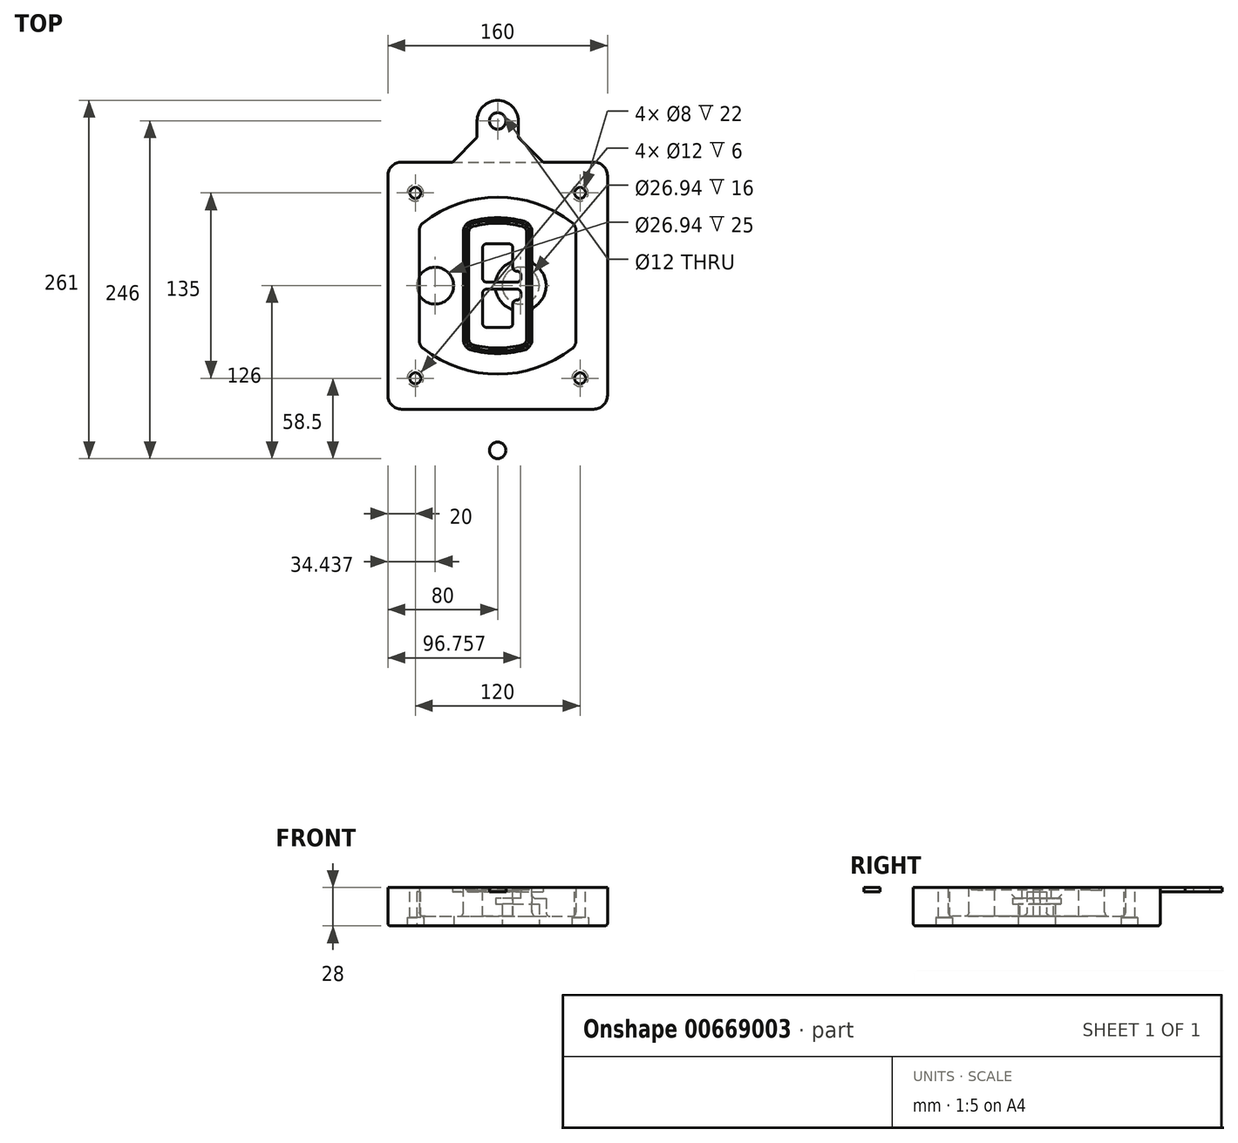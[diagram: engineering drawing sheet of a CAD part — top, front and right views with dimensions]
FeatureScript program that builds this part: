
annotation { "Feature Type Name" : "Feature", "Feature Type Description" : "" }
export const myFeature = defineFeature(function(context is Context, id is Id, definition is map)
    precondition{}
    {
        {
            var Q0;
            Q0=qCreatedBy(makeId("Top.planeOp"),FACE);
            var sketch = newSketch(context, id + "F0", { "sketchPlane" : qUnion([Q0])});
            skPoint(sketch, "E0.rect.middle", {"position": v(0, 0) * mm});
            skLineSegment(sketch, "E1.bottom", {"start": v(-70, -90) * mm, "end": v(70, -90) * mm});
            skLineSegment(sketch, "E1.top", {"start": v(-70, 90) * mm, "end": v(70, 90) * mm});
            skLineSegment(sketch, "E1.left", {"start": v(-80, -80) * mm, "end": v(-80, 80) * mm});
            skLineSegment(sketch, "E1.right", {"start": v(80, -80) * mm, "end": v(80, 80) * mm});
            skLineSegment(sketch, "E2", {"start": v(-80, 90) * mm, "end": v(80, -90) * mm, "construction": true});
            skLineSegment(sketch, "E3", {"start": v(80, 90) * mm, "end": v(-80, -90) * mm, "construction": true});
            skCircle(sketch, "E4", {"center": v(-60, 67.5) * mm, "radius": 4 * mm});
            skCircle(sketch, "E5", {"center": v(60, 67.5) * mm, "radius": 4 * mm});
            skCircle(sketch, "E6", {"center": v(60, -67.5) * mm, "radius": 4 * mm});
            skCircle(sketch, "E7", {"center": v(-60, -67.5) * mm, "radius": 4 * mm});
            skLineSegment(sketch, "E8", {"start": v(-60, 67.5) * mm, "end": v(60, 67.5) * mm, "construction": true});
            skLineSegment(sketch, "E9", {"start": v(60, 67.5) * mm, "end": v(60, -67.5) * mm, "construction": true});
            skLineSegment(sketch, "E10", {"start": v(60, -67.5) * mm, "end": v(-60, -67.5) * mm, "construction": true});
            skLineSegment(sketch, "E11", {"start": v(-60, -67.5) * mm, "end": v(-60, 67.5) * mm, "construction": true});
            skLineSegment(sketch, "E12", {"start": v(-60, 40.3) * mm, "end": v(-60, -40.3) * mm});
            skLineSegment(sketch, "E13", {"start": v(60, 40.3) * mm, "end": v(60, -40.3) * mm});
            skArc(sketch, "E14", {"start": v(56.15, 48.18) * mm, "mid": v(0, 67.5) * mm, "end": v(-56.15, 48.18) * mm});
            skArc(sketch, "E15", {"start": v(-56.15, -48.18) * mm, "mid": v(0, -67.5) * mm, "end": v(56.15, -48.18) * mm});
            skLineSegment(sketch, "E16", {"start": v(-60, 0) * mm, "end": v(60, 0) * mm, "construction": true});
            skPoint(sketch, "E17.visualSharp", {"position": v(-60, -45) * mm});
            skArc(sketch, "E17.filletArc", {"start": v(-60, -40.3) * mm, "mid": v(-58.99, -44.68) * mm, "end": v(-56.15, -48.18) * mm});
            skPoint(sketch, "E18.visualSharp", {"position": v(-60, 45) * mm});
            skArc(sketch, "E18.filletArc", {"start": v(-56.15, 48.18) * mm, "mid": v(-58.99, 44.68) * mm, "end": v(-60, 40.3) * mm});
            skPoint(sketch, "E19.visualSharp", {"position": v(60, 45) * mm});
            skArc(sketch, "E19.filletArc", {"start": v(60, 40.3) * mm, "mid": v(58.99, 44.68) * mm, "end": v(56.15, 48.18) * mm});
            skPoint(sketch, "E20.visualSharp", {"position": v(60, -45) * mm});
            skArc(sketch, "E20.filletArc", {"start": v(56.15, -48.18) * mm, "mid": v(58.99, -44.68) * mm, "end": v(60, -40.3) * mm});
            skPoint(sketch, "E21.visualSharp", {"position": v(-80, 90) * mm});
            skArc(sketch, "E21.filletArc", {"start": v(-70, 90) * mm, "mid": v(-77.07, 87.07) * mm, "end": v(-80, 80) * mm});
            skPoint(sketch, "E22.visualSharp", {"position": v(80, 90) * mm});
            skArc(sketch, "E22.filletArc", {"start": v(80, 80) * mm, "mid": v(77.07, 87.07) * mm, "end": v(70, 90) * mm});
            skPoint(sketch, "E23.visualSharp", {"position": v(80, -90) * mm});
            skArc(sketch, "E23.filletArc", {"start": v(70, -90) * mm, "mid": v(77.07, -87.07) * mm, "end": v(80, -80) * mm});
            skPoint(sketch, "E24.visualSharp", {"position": v(-80, -90) * mm});
            skArc(sketch, "E24.filletArc", {"start": v(-80, -80) * mm, "mid": v(-77.07, -87.07) * mm, "end": v(-70, -90) * mm});
            skArc(sketch, "E25.0", {"start": v(57, 40.3) * mm, "mid": v(56.3, 43.36) * mm, "end": v(54.3, 45.81) * mm});
            skLineSegment(sketch, "E25.1", {"start": v(57, 40.3) * mm, "end": v(57, -40.3) * mm});
            skArc(sketch, "E25.2", {"start": v(54.3, -45.81) * mm, "mid": v(56.3, -43.36) * mm, "end": v(57, -40.3) * mm});
            skArc(sketch, "E25.3", {"start": v(-54.3, -45.81) * mm, "mid": v(0, -64.5) * mm, "end": v(54.3, -45.81) * mm});
            skArc(sketch, "E25.4", {"start": v(-57, -40.3) * mm, "mid": v(-56.3, -43.36) * mm, "end": v(-54.3, -45.81) * mm});
            skArc(sketch, "E25.5", {"start": v(54.3, 45.81) * mm, "mid": v(0, 64.5) * mm, "end": v(-54.3, 45.81) * mm});
            skLineSegment(sketch, "E25.6", {"start": v(-57, 40.3) * mm, "end": v(-57, -40.3) * mm});
            skArc(sketch, "E25.7", {"start": v(-54.3, 45.81) * mm, "mid": v(-56.3, 43.36) * mm, "end": v(-57, 40.3) * mm});
            skArc(sketch, "E26.0", {"start": v(-58.62, 51.33) * mm, "mid": v(-62.58, 46.43) * mm, "end": v(-64, 40.3) * mm});
            skArc(sketch, "E26.1", {"start": v(58.62, 51.33) * mm, "mid": v(0, 71.5) * mm, "end": v(-58.62, 51.33) * mm});
            skArc(sketch, "E26.2", {"start": v(64, 40.3) * mm, "mid": v(62.58, 46.43) * mm, "end": v(58.62, 51.33) * mm});
            skLineSegment(sketch, "E26.3", {"start": v(64, 40.3) * mm, "end": v(64, -40.3) * mm});
            skArc(sketch, "E26.4", {"start": v(58.62, -51.33) * mm, "mid": v(62.58, -46.43) * mm, "end": v(64, -40.3) * mm});
            skLineSegment(sketch, "E26.5", {"start": v(-64, 40.3) * mm, "end": v(-64, -40.3) * mm});
            skArc(sketch, "E26.6", {"start": v(-58.62, -51.33) * mm, "mid": v(0, -71.5) * mm, "end": v(58.62, -51.33) * mm});
            skArc(sketch, "E26.7", {"start": v(-64, -40.3) * mm, "mid": v(-62.58, -46.43) * mm, "end": v(-58.62, -51.33) * mm});
            skSolve(sketch);
        }
        {
            var Q0;
            Q0=makeQuery(id+"F0.imprint","IMPRINT",FACE,{"disambiguationData":[TD([[makeQuery(id+"F0.imprint","IMPRINT",EDGE,{"derivedFrom":sQuery(id+"F0.wireOp",EDGE,"E1.bottom")}),1.0]])]});
            var Q1;
            Q1=makeQuery(id+"F0.imprint","IMPRINT",FACE,{"disambiguationData":[TD([[makeQuery(id+"F0.imprint","IMPRINT",EDGE,{"derivedFrom":sQuery(id+"F0.wireOp",EDGE,"E12")}),1.0]])]});
            var Q2;
            Q2=makeQuery(id+"F0.imprint","IMPRINT",FACE,{"disambiguationData":[TD([[makeQuery(id+"F0.imprint","IMPRINT",EDGE,{"derivedFrom":sQuery(id+"F0.wireOp",EDGE,"E25.0")}),1.0]])]});
            var Q3;
            Q3=makeQuery(id+"F0.imprint","IMPRINT",FACE,{"disambiguationData":[TD([[makeQuery(id+"F0.imprint","IMPRINT",EDGE,{"derivedFrom":sQuery(id+"F0.wireOp",EDGE,"E12")}),-1.0]])]});
            extrude(context, id + "F1", {"entities" : qUnion([Q0, Q1, Q2, Q3]), "oppositeDirection" : true, "depth" : 25 * mm});
        }
        {
            var Q0;
            Q0=makeQuery(id+"F0.imprint","IMPRINT",FACE,{"disambiguationData":[TD([[makeQuery(id+"F0.imprint","IMPRINT",EDGE,{"derivedFrom":sQuery(id+"F0.wireOp",EDGE,"E12")}),1.0]])]});
            extrude(context, id + "F2", {"entities" : qUnion([Q0]), "operationType" : NewBodyOperationType.ADD, "depth" : 3 * mm});
        }
        {
            var Q0;
            Q0=makeQuery(id+"F0.imprint","IMPRINT",FACE,{"disambiguationData":[TD([[makeQuery(id+"F0.imprint","IMPRINT",EDGE,{"derivedFrom":sQuery(id+"F0.wireOp",EDGE,"E25.0")}),1.0]])]});
            extrude(context, id + "F3", {"entities" : qUnion([Q0]), "operationType" : NewBodyOperationType.REMOVE, "oppositeDirection" : true, "depth" : 18 * mm});
        }
        {
            var Q0;
            Q0=makeQuery(id+"F2.opExtrude","CAP_FACE",FACE,{"disambiguationData":[OSD([sQuery(id+"F0.wireOp",EDGE,"E12"),sQuery(id+"F0.wireOp",EDGE,"E13"),sQuery(id+"F0.wireOp",EDGE,"E14"),sQuery(id+"F0.wireOp",EDGE,"E15"),sQuery(id+"F0.wireOp",EDGE,"E17.filletArc"),sQuery(id+"F0.wireOp",EDGE,"E18.filletArc"),sQuery(id+"F0.wireOp",EDGE,"E19.filletArc"),sQuery(id+"F0.wireOp",EDGE,"E20.filletArc"),sQuery(id+"F0.wireOp",EDGE,"E25.0"),sQuery(id+"F0.wireOp",EDGE,"E25.1"),sQuery(id+"F0.wireOp",EDGE,"E25.2"),sQuery(id+"F0.wireOp",EDGE,"E25.3"),sQuery(id+"F0.wireOp",EDGE,"E25.4"),sQuery(id+"F0.wireOp",EDGE,"E25.5"),sQuery(id+"F0.wireOp",EDGE,"E25.6"),sQuery(id+"F0.wireOp",EDGE,"E25.7")])],"isStart":false});
            var sketch = newSketch(context, id + "F4", { "sketchPlane" : qUnion([Q0])});
            skArc(sketch, "E27.0", {"start": v(-19.08, -46.97) * mm, "mid": v(0, -49.5) * mm, "end": v(19.08, -46.97) * mm});
            skArc(sketch, "E28.0", {"start": v(19.08, 46.97) * mm, "mid": v(0, 49.5) * mm, "end": v(-19.08, 46.97) * mm});
            skLineSegment(sketch, "E29", {"start": v(-25, 39.25) * mm, "end": v(-25, -39.25) * mm});
            skLineSegment(sketch, "E30", {"start": v(25, 39.25) * mm, "end": v(25, -39.25) * mm});
            skLineSegment(sketch, "E31", {"start": v(-25, 45.1) * mm, "end": v(25, 45.1) * mm, "construction": true});
            skLineSegment(sketch, "E32", {"start": v(-25, -45.1) * mm, "end": v(25, -45.1) * mm, "construction": true});
            skPoint(sketch, "E33.visualSharp", {"position": v(-25, 45.1) * mm});
            skArc(sketch, "E33.filletArc", {"start": v(-19.08, 46.97) * mm, "mid": v(-23.35, 44.11) * mm, "end": v(-25, 39.25) * mm});
            skPoint(sketch, "E34.visualSharp", {"position": v(25, 45.1) * mm});
            skArc(sketch, "E34.filletArc", {"start": v(25, 39.25) * mm, "mid": v(23.35, 44.11) * mm, "end": v(19.08, 46.97) * mm});
            skPoint(sketch, "E35.visualSharp", {"position": v(25, -45.1) * mm});
            skArc(sketch, "E35.filletArc", {"start": v(19.08, -46.97) * mm, "mid": v(23.35, -44.11) * mm, "end": v(25, -39.25) * mm});
            skPoint(sketch, "E36.visualSharp", {"position": v(-25, -45.1) * mm});
            skArc(sketch, "E36.filletArc", {"start": v(-25, -39.25) * mm, "mid": v(-23.35, -44.11) * mm, "end": v(-19.08, -46.97) * mm});
            skArc(sketch, "E37.0", {"start": v(54.3, 45.81) * mm, "mid": v(0, 64.5) * mm, "end": v(-54.3, 45.81) * mm});
            skArc(sketch, "E37.1", {"start": v(-54.3, 45.81) * mm, "mid": v(-56.3, 43.36) * mm, "end": v(-57, 40.3) * mm});
            skLineSegment(sketch, "E37.2", {"start": v(-57, 40.3) * mm, "end": v(-57, -40.3) * mm});
            skArc(sketch, "E37.3", {"start": v(-57, -40.3) * mm, "mid": v(-56.3, -43.36) * mm, "end": v(-54.3, -45.81) * mm});
            skArc(sketch, "E37.4", {"start": v(-54.3, -45.81) * mm, "mid": v(0, -64.5) * mm, "end": v(54.3, -45.81) * mm});
            skArc(sketch, "E37.5", {"start": v(54.3, -45.81) * mm, "mid": v(56.3, -43.36) * mm, "end": v(57, -40.3) * mm});
            skLineSegment(sketch, "E37.6", {"start": v(57, 40.3) * mm, "end": v(57, -40.3) * mm});
            skArc(sketch, "E37.7", {"start": v(57, 40.3) * mm, "mid": v(56.3, 43.36) * mm, "end": v(54.3, 45.81) * mm});
            skLineSegment(sketch, "E38.0", {"start": v(23, 39.25) * mm, "end": v(23, -39.25) * mm});
            skArc(sketch, "E38.1", {"start": v(18.56, -45.04) * mm, "mid": v(21.76, -42.9) * mm, "end": v(23, -39.25) * mm});
            skArc(sketch, "E38.2", {"start": v(-18.56, -45.04) * mm, "mid": v(0, -47.5) * mm, "end": v(18.56, -45.04) * mm});
            skArc(sketch, "E38.3", {"start": v(-23, -39.25) * mm, "mid": v(-21.76, -42.9) * mm, "end": v(-18.56, -45.04) * mm});
            skLineSegment(sketch, "E38.4", {"start": v(-23, 39.25) * mm, "end": v(-23, -39.25) * mm});
            skArc(sketch, "E38.5", {"start": v(23, 39.25) * mm, "mid": v(21.76, 42.9) * mm, "end": v(18.56, 45.04) * mm});
            skArc(sketch, "E38.6", {"start": v(-18.56, 45.04) * mm, "mid": v(-21.76, 42.9) * mm, "end": v(-23, 39.25) * mm});
            skArc(sketch, "E38.7", {"start": v(18.56, 45.04) * mm, "mid": v(0, 47.5) * mm, "end": v(-18.56, 45.04) * mm});
            skArc(sketch, "E39.0", {"start": v(21, 39.25) * mm, "mid": v(20.18, 41.68) * mm, "end": v(18.04, 43.1) * mm});
            skLineSegment(sketch, "E39.1", {"start": v(21, 39.25) * mm, "end": v(21, -39.25) * mm});
            skArc(sketch, "E39.2", {"start": v(18.04, -43.1) * mm, "mid": v(20.18, -41.68) * mm, "end": v(21, -39.25) * mm});
            skArc(sketch, "E39.3", {"start": v(-18.04, -43.1) * mm, "mid": v(0, -45.5) * mm, "end": v(18.04, -43.1) * mm});
            skArc(sketch, "E39.4", {"start": v(-21, -39.25) * mm, "mid": v(-20.18, -41.68) * mm, "end": v(-18.04, -43.1) * mm});
            skArc(sketch, "E39.5", {"start": v(18.04, 43.1) * mm, "mid": v(0, 45.5) * mm, "end": v(-18.04, 43.1) * mm});
            skLineSegment(sketch, "E39.6", {"start": v(-21, 39.25) * mm, "end": v(-21, -39.25) * mm});
            skArc(sketch, "E39.7", {"start": v(-18.04, 43.1) * mm, "mid": v(-20.18, 41.68) * mm, "end": v(-21, 39.25) * mm});
            skLineSegment(sketch, "E40", {"start": v(-25, 0) * mm, "end": v(25, 0) * mm, "construction": true});
            skLineSegment(sketch, "E41", {"start": v(-11, 5.5) * mm, "end": v(-11, 27.5) * mm});
            skLineSegment(sketch, "E42", {"start": v(-8, 30.5) * mm, "end": v(8, 30.5) * mm});
            skLineSegment(sketch, "E43", {"start": v(11, 27.5) * mm, "end": v(11, 13.5) * mm});
            skLineSegment(sketch, "E44", {"start": v(14, 10.5) * mm, "end": v(14, 10.5) * mm});
            skLineSegment(sketch, "E45", {"start": v(17, 7.5) * mm, "end": v(17, 5.5) * mm});
            skLineSegment(sketch, "E46", {"start": v(14, 2.5) * mm, "end": v(-8, 2.5) * mm});
            skPoint(sketch, "E47.visualSharp", {"position": v(-11, 30.5) * mm});
            skArc(sketch, "E47.filletArc", {"start": v(-8, 30.5) * mm, "mid": v(-10.12, 29.62) * mm, "end": v(-11, 27.5) * mm});
            skPoint(sketch, "E48.visualSharp", {"position": v(11, 30.5) * mm});
            skArc(sketch, "E48.filletArc", {"start": v(11, 27.5) * mm, "mid": v(10.12, 29.62) * mm, "end": v(8, 30.5) * mm});
            skPoint(sketch, "E49.visualSharp", {"position": v(11, 10.5) * mm});
            skArc(sketch, "E49.filletArc", {"start": v(11, 13.5) * mm, "mid": v(11.88, 11.38) * mm, "end": v(14, 10.5) * mm});
            skPoint(sketch, "E50.visualSharp", {"position": v(17, 10.5) * mm});
            skArc(sketch, "E50.filletArc", {"start": v(17, 7.5) * mm, "mid": v(16.12, 9.62) * mm, "end": v(14, 10.5) * mm});
            skPoint(sketch, "E51.visualSharp", {"position": v(17, 2.5) * mm});
            skArc(sketch, "E51.filletArc", {"start": v(14, 2.5) * mm, "mid": v(16.12, 3.38) * mm, "end": v(17, 5.5) * mm});
            skPoint(sketch, "E52.visualSharp", {"position": v(-11, 2.5) * mm});
            skArc(sketch, "E52.filletArc", {"start": v(-11, 5.5) * mm, "mid": v(-10.12, 3.38) * mm, "end": v(-8, 2.5) * mm});
            skLineSegment(sketch, "E53.0.MirrorCS", {"start": v(14, -2.5) * mm, "end": v(-8, -2.5) * mm});
            skArc(sketch, "E54.0.MirrorCS", {"start": v(-11, -5.5) * mm, "mid": v(-10.12, -3.38) * mm, "end": v(-8, -2.5) * mm});
            skLineSegment(sketch, "E55.0.MirrorCS", {"start": v(-11, -5.5) * mm, "end": v(-11, -27.5) * mm});
            skArc(sketch, "E56.0.MirrorCS", {"start": v(-8, -30.5) * mm, "mid": v(-10.12, -29.62) * mm, "end": v(-11, -27.5) * mm});
            skLineSegment(sketch, "E57.0.MirrorCS", {"start": v(-8, -30.5) * mm, "end": v(8, -30.5) * mm});
            skArc(sketch, "E58.0.MirrorCS", {"start": v(11, -27.5) * mm, "mid": v(10.12, -29.62) * mm, "end": v(8, -30.5) * mm});
            skLineSegment(sketch, "E59.0.MirrorCS", {"start": v(11, -27.5) * mm, "end": v(11, -13.5) * mm});
            skArc(sketch, "E60.0.MirrorCS", {"start": v(11, -13.5) * mm, "mid": v(11.88, -11.38) * mm, "end": v(14, -10.5) * mm});
            skArc(sketch, "E61.0.MirrorCS", {"start": v(17, -7.5) * mm, "mid": v(16.12, -9.62) * mm, "end": v(14, -10.5) * mm});
            skLineSegment(sketch, "E62.0.MirrorCS", {"start": v(17, -7.5) * mm, "end": v(17, -5.5) * mm});
            skArc(sketch, "E63.0.MirrorCS", {"start": v(14, -2.5) * mm, "mid": v(16.12, -3.38) * mm, "end": v(17, -5.5) * mm});
            skSolve(sketch);
        }
        {
            var Q0;
            Q0=makeQuery(id+"F4.imprint","IMPRINT",FACE,{"disambiguationData":[TD([[makeQuery(id+"F4.imprint","IMPRINT",EDGE,{"derivedFrom":sQuery(id+"F4.wireOp",EDGE,"E27.0")}),1.0]])]});
            var Q1;
            Q1=makeQuery(id+"F4.imprint","IMPRINT",FACE,{"disambiguationData":[TD([[makeQuery(id+"F4.imprint","IMPRINT",EDGE,{"derivedFrom":sQuery(id+"F4.wireOp",EDGE,"E38.0")}),-1.0]])]});
            var Q2;
            Q2=makeQuery(id+"F4.imprint","IMPRINT",FACE,{"disambiguationData":[TD([[makeQuery(id+"F4.imprint","IMPRINT",EDGE,{"derivedFrom":sQuery(id+"F4.wireOp",EDGE,"E39.0")}),1.0]])]});
            extrude(context, id + "F5", {"entities" : qUnion([Q0, Q1, Q2]), "operationType" : NewBodyOperationType.ADD, "endBound" : BoundingType.UP_TO_NEXT, "oppositeDirection" : true, "depth" : 25 * mm});
        }
        {
            var Q0;
            Q0=makeQuery(id+"F4.imprint","IMPRINT",FACE,{"disambiguationData":[TD([[makeQuery(id+"F4.imprint","IMPRINT",EDGE,{"derivedFrom":sQuery(id+"F4.wireOp",EDGE,"E38.0")}),-1.0]])]});
            extrude(context, id + "F6", {"entities" : qUnion([Q0]), "operationType" : NewBodyOperationType.REMOVE, "oppositeDirection" : true, "depth" : 2 * mm});
        }
        {
            var Q0;
            Q0=makeQuery(id+"F1.opExtrude","CAP_FACE",FACE,{"disambiguationData":[OSD([sQuery(id+"F0.wireOp",EDGE,"E1.bottom"),sQuery(id+"F0.wireOp",EDGE,"E1.top"),sQuery(id+"F0.wireOp",EDGE,"E1.left"),sQuery(id+"F0.wireOp",EDGE,"E1.right"),sQuery(id+"F0.wireOp",EDGE,"E4"),sQuery(id+"F0.wireOp",EDGE,"E5"),sQuery(id+"F0.wireOp",EDGE,"E6"),sQuery(id+"F0.wireOp",EDGE,"E7"),sQuery(id+"F0.wireOp",EDGE,"E21.filletArc"),sQuery(id+"F0.wireOp",EDGE,"E22.filletArc"),sQuery(id+"F0.wireOp",EDGE,"E23.filletArc"),sQuery(id+"F0.wireOp",EDGE,"E24.filletArc")])],"isStart":false});
            var sketch = newSketch(context, id + "F7", { "sketchPlane" : qUnion([Q0])});
            skCircle(sketch, "E64", {"center": v(16.76, 0) * mm, "radius": 13.47 * mm});
            skCircle(sketch, "E65", {"center": v(-45.56, 0) * mm, "radius": 13.47 * mm});
            skLineSegment(sketch, "E66", {"start": v(80, 0) * mm, "end": v(-80, 0) * mm});
            skCircle(sketch, "E67", {"center": v(16.76, 0) * mm, "radius": 18.47 * mm});
            skCircle(sketch, "E68", {"center": v(60, -67.5) * mm, "radius": 6 * mm});
            skCircle(sketch, "E69", {"center": v(-60, -67.5) * mm, "radius": 6 * mm});
            skCircle(sketch, "E70", {"center": v(-60, 67.5) * mm, "radius": 6 * mm});
            skCircle(sketch, "E71", {"center": v(60, 67.5) * mm, "radius": 6 * mm});
            skSolve(sketch);
        }
        {
            var Q0;
            {var subQ1=sQuery(id+"F7.wireOp",EDGE,"E66");var subQ4=sQuery(id+"F7.wireOp",EDGE,"E64");var subQ6=makeQuery(id+"F7.imprint","INTERSECT",VERTEX,{"disambiguationData":[OD(0.0)],"derivedFrom":[subQ4,subQ1]});Q0=makeQuery(id+"F7.imprint","IMPRINT",FACE,{"disambiguationData":[TD([[makeQuery(id+"F7.imprint","IMPRINT",EDGE,{"disambiguationData":[TD([[subQ6,-1.0]])],"derivedFrom":subQ4}),-1.0]])]});}
            var Q1;
            {var subQ0=sQuery(id+"F7.wireOp",EDGE,"E66");var subQ1=sQuery(id+"F7.wireOp",EDGE,"E64");var subQ3=makeQuery(id+"F7.imprint","INTERSECT",VERTEX,{"disambiguationData":[OD(0.0)],"derivedFrom":[subQ1,subQ0]});Q1=makeQuery(id+"F7.imprint","IMPRINT",FACE,{"disambiguationData":[TD([[makeQuery(id+"F7.imprint","IMPRINT",EDGE,{"disambiguationData":[TD([[subQ3,-1.0]])],"derivedFrom":subQ1}),1.0]])]});}
            var Q2;
            {var subQ0=sQuery(id+"F7.wireOp",EDGE,"E66");var subQ1=sQuery(id+"F7.wireOp",EDGE,"E64");var subQ3=makeQuery(id+"F7.imprint","INTERSECT",VERTEX,{"disambiguationData":[OD(0.0)],"derivedFrom":[subQ1,subQ0]});Q2=makeQuery(id+"F7.imprint","IMPRINT",FACE,{"disambiguationData":[TD([[makeQuery(id+"F7.imprint","IMPRINT",EDGE,{"disambiguationData":[TD([[subQ3,1.0]])],"derivedFrom":subQ1}),1.0]])]});}
            var Q3;
            {var subQ1=sQuery(id+"F7.wireOp",EDGE,"E66");var subQ4=sQuery(id+"F7.wireOp",EDGE,"E64");var subQ6=makeQuery(id+"F7.imprint","INTERSECT",VERTEX,{"disambiguationData":[OD(0.0)],"derivedFrom":[subQ4,subQ1]});Q3=makeQuery(id+"F7.imprint","IMPRINT",FACE,{"disambiguationData":[TD([[makeQuery(id+"F7.imprint","IMPRINT",EDGE,{"disambiguationData":[TD([[subQ6,1.0]])],"derivedFrom":subQ4}),-1.0]])]});}
            extrude(context, id + "F8", {"entities" : qUnion([Q0, Q1, Q2, Q3]), "operationType" : NewBodyOperationType.ADD, "oppositeDirection" : true, "depth" : 20 * mm});
        }
        {
            var Q0;
            {var subQ0=sQuery(id+"F7.wireOp",EDGE,"E66");var subQ1=sQuery(id+"F7.wireOp",EDGE,"E64");var subQ3=makeQuery(id+"F7.imprint","INTERSECT",VERTEX,{"disambiguationData":[OD(0.0)],"derivedFrom":[subQ1,subQ0]});Q0=makeQuery(id+"F7.imprint","IMPRINT",FACE,{"disambiguationData":[TD([[makeQuery(id+"F7.imprint","IMPRINT",EDGE,{"disambiguationData":[TD([[subQ3,-1.0]])],"derivedFrom":subQ1}),1.0]])]});}
            var Q1;
            {var subQ0=sQuery(id+"F7.wireOp",EDGE,"E66");var subQ1=sQuery(id+"F7.wireOp",EDGE,"E64");var subQ3=makeQuery(id+"F7.imprint","INTERSECT",VERTEX,{"disambiguationData":[OD(0.0)],"derivedFrom":[subQ1,subQ0]});Q1=makeQuery(id+"F7.imprint","IMPRINT",FACE,{"disambiguationData":[TD([[makeQuery(id+"F7.imprint","IMPRINT",EDGE,{"disambiguationData":[TD([[subQ3,1.0]])],"derivedFrom":subQ1}),1.0]])]});}
            extrude(context, id + "F9", {"entities" : qUnion([Q0, Q1]), "operationType" : NewBodyOperationType.REMOVE, "oppositeDirection" : true, "depth" : 16 * mm});
        }
        {
            var Q0;
            {var subQ0=sQuery(id+"F7.wireOp",EDGE,"E66");var subQ1=sQuery(id+"F7.wireOp",EDGE,"E65");var subQ3=makeQuery(id+"F7.imprint","INTERSECT",VERTEX,{"disambiguationData":[OD(0.0)],"derivedFrom":[subQ1,subQ0]});Q0=makeQuery(id+"F7.imprint","IMPRINT",FACE,{"disambiguationData":[TD([[makeQuery(id+"F7.imprint","IMPRINT",EDGE,{"disambiguationData":[TD([[subQ3,-1.0]])],"derivedFrom":subQ1}),1.0]])]});}
            var Q1;
            {var subQ0=sQuery(id+"F7.wireOp",EDGE,"E66");var subQ1=sQuery(id+"F7.wireOp",EDGE,"E65");var subQ3=makeQuery(id+"F7.imprint","INTERSECT",VERTEX,{"disambiguationData":[OD(0.0)],"derivedFrom":[subQ1,subQ0]});Q1=makeQuery(id+"F7.imprint","IMPRINT",FACE,{"disambiguationData":[TD([[makeQuery(id+"F7.imprint","IMPRINT",EDGE,{"disambiguationData":[TD([[subQ3,1.0]])],"derivedFrom":subQ1}),1.0]])]});}
            extrude(context, id + "F10", {"entities" : qUnion([Q0, Q1]), "operationType" : NewBodyOperationType.REMOVE, "oppositeDirection" : true, "depth" : 25 * mm});
        }
        {
            var Q0;
            Q0=makeQuery(id+"F7.imprint","IMPRINT",FACE,{"disambiguationData":[TD([[makeQuery(id+"F7.imprint","IMPRINT",EDGE,{"derivedFrom":sQuery(id+"F7.wireOp",EDGE,"E68")}),1.0]])]});
            var Q1;
            Q1=makeQuery(id+"F7.imprint","IMPRINT",FACE,{"disambiguationData":[TD([[makeQuery(id+"F7.imprint","IMPRINT",EDGE,{"derivedFrom":makeQuery(id+"F1.opExtrude","CAP_EDGE",EDGE,{"disambiguationData":[OSD([sQuery(id+"F0.wireOp",EDGE,"E5")])],"isStart":false})}),-1.0]])]});
            var Q2;
            Q2=makeQuery(id+"F7.imprint","IMPRINT",FACE,{"disambiguationData":[TD([[makeQuery(id+"F7.imprint","IMPRINT",EDGE,{"derivedFrom":sQuery(id+"F7.wireOp",EDGE,"E69")}),1.0]])]});
            var Q3;
            Q3=makeQuery(id+"F7.imprint","IMPRINT",FACE,{"disambiguationData":[TD([[makeQuery(id+"F7.imprint","IMPRINT",EDGE,{"derivedFrom":makeQuery(id+"F1.opExtrude","CAP_EDGE",EDGE,{"disambiguationData":[OSD([sQuery(id+"F0.wireOp",EDGE,"E4")])],"isStart":false})}),-1.0]])]});
            var Q4;
            Q4=makeQuery(id+"F7.imprint","IMPRINT",FACE,{"disambiguationData":[TD([[makeQuery(id+"F7.imprint","IMPRINT",EDGE,{"derivedFrom":sQuery(id+"F7.wireOp",EDGE,"E70")}),1.0]])]});
            var Q5;
            Q5=makeQuery(id+"F7.imprint","IMPRINT",FACE,{"disambiguationData":[TD([[makeQuery(id+"F7.imprint","IMPRINT",EDGE,{"derivedFrom":makeQuery(id+"F1.opExtrude","CAP_EDGE",EDGE,{"disambiguationData":[OSD([sQuery(id+"F0.wireOp",EDGE,"E7")])],"isStart":false})}),-1.0]])]});
            var Q6;
            Q6=makeQuery(id+"F7.imprint","IMPRINT",FACE,{"disambiguationData":[TD([[makeQuery(id+"F7.imprint","IMPRINT",EDGE,{"derivedFrom":sQuery(id+"F7.wireOp",EDGE,"E71")}),1.0]])]});
            var Q7;
            Q7=makeQuery(id+"F7.imprint","IMPRINT",FACE,{"disambiguationData":[TD([[makeQuery(id+"F7.imprint","IMPRINT",EDGE,{"derivedFrom":makeQuery(id+"F1.opExtrude","CAP_EDGE",EDGE,{"disambiguationData":[OSD([sQuery(id+"F0.wireOp",EDGE,"E6")])],"isStart":false})}),-1.0]])]});
            extrude(context, id + "F11", {"entities" : qUnion([Q0, Q1, Q2, Q3, Q4, Q5, Q6, Q7]), "operationType" : NewBodyOperationType.REMOVE, "oppositeDirection" : true, "depth" : 6 * mm});
        }
        {
            var Q0;
            Q0=makeQuery(id+"F9.boolean.opBoolean","COPY",FACE,{"derivedFrom":makeQuery(id+"F9.opExtrude","CAP_FACE",FACE,{"disambiguationData":[OSD([sQuery(id+"F7.wireOp",EDGE,"E64")])],"isStart":false})});
            var sketch = newSketch(context, id + "F12", { "sketchPlane" : qUnion([Q0])});
            skArc(sketch, "E72.0", {"start": v(11, 17.55) * mm, "mid": v(2.57, 11.82) * mm, "end": v(-1.54, 2.5) * mm});
            skArc(sketch, "E72.1", {"start": v(-1.54, -2.5) * mm, "mid": v(2.57, -11.82) * mm, "end": v(11, -17.55) * mm});
            skLineSegment(sketch, "E73", {"start": v(-1.54, -2.5) * mm, "end": v(14, -2.5) * mm});
            skLineSegment(sketch, "E74.0", {"start": v(14, 2.5) * mm, "end": v(-1.54, 2.5) * mm});
            skArc(sketch, "E74.1", {"start": v(14, 2.5) * mm, "mid": v(16.12, 3.38) * mm, "end": v(17, 5.5) * mm});
            skLineSegment(sketch, "E74.2", {"start": v(17, 7.5) * mm, "end": v(17, 5.5) * mm});
            skArc(sketch, "E74.3", {"start": v(17, 7.5) * mm, "mid": v(16.12, 9.62) * mm, "end": v(14, 10.5) * mm});
            skArc(sketch, "E74.4", {"start": v(11, 13.5) * mm, "mid": v(11.88, 11.38) * mm, "end": v(14, 10.5) * mm});
            skLineSegment(sketch, "E74.5", {"start": v(11, 17.55) * mm, "end": v(11, 13.5) * mm});
            skLineSegment(sketch, "E74.7", {"start": v(14, -2.5) * mm, "end": v(-1.54, -2.5) * mm});
            skArc(sketch, "E74.8", {"start": v(14, -2.5) * mm, "mid": v(16.12, -3.38) * mm, "end": v(17, -5.5) * mm});
            skLineSegment(sketch, "E74.9", {"start": v(17, -7.5) * mm, "end": v(17, -5.5) * mm});
            skArc(sketch, "E74.10", {"start": v(17, -7.5) * mm, "mid": v(16.12, -9.62) * mm, "end": v(14, -10.5) * mm});
            skArc(sketch, "E74.11", {"start": v(11, -13.5) * mm, "mid": v(11.88, -11.38) * mm, "end": v(14, -10.5) * mm});
            skLineSegment(sketch, "E74.12", {"start": v(11, -17.55) * mm, "end": v(11, -13.5) * mm});
            skPoint(sketch, "E75.orphan", {"position": v(11, -27.5) * mm});
            skPoint(sketch, "E76.orphan", {"position": v(-8, -2.5) * mm});
            skPoint(sketch, "E77.orphan", {"position": v(-8, 2.5) * mm});
            skPoint(sketch, "E78.orphan", {"position": v(11, 27.5) * mm});
            skSolve(sketch);
        }
        {
            var Q0;
            {var subQ7=sQuery(id+"F12.wireOp",EDGE,"E72.0");var subQ14=sQuery(id+"F12.wireOp",EDGE,"E72.1");var subQ16=sQuery(id+"F12.wireOp",EDGE,"E74.1");var subQ18=sQuery(id+"F12.wireOp",EDGE,"E74.8");Q0=qUnion([makeQuery(id+"F12.imprint","IMPRINT",FACE,{"disambiguationData":[TD([[makeQuery(id+"F12.imprint","IMPRINT",EDGE,{"derivedFrom":subQ7}),1.0]])]}),makeQuery(id+"F12.imprint","IMPRINT",FACE,{"disambiguationData":[TD([[makeQuery(id+"F12.imprint","IMPRINT",EDGE,{"derivedFrom":subQ14}),1.0]])]}),makeQuery(id+"F12.imprint","IMPRINT",FACE,{"disambiguationData":[TD([[makeQuery(id+"F12.imprint","IMPRINT",EDGE,{"derivedFrom":subQ16}),1.0]])]}),makeQuery(id+"F12.imprint","IMPRINT",FACE,{"disambiguationData":[TD([[makeQuery(id+"F12.imprint","IMPRINT",EDGE,{"derivedFrom":subQ18}),-1.0]])]})]);}
            var Q1;
            Q1=makeQuery(id+"F5.boolean.opBoolean","SPLIT",FACE,{"disambiguationData":[TD([makeQuery(id+"F5.opExtrude","SWEPT_FACE",FACE,{"disambiguationData":[OSD([sQuery(id+"F4.wireOp",EDGE,"E41")])]})])],"derivedFrom":makeQuery(id+"F3.boolean.opBoolean","COPY",FACE,{"derivedFrom":makeQuery(id+"F3.opExtrude","CAP_FACE",FACE,{"disambiguationData":[OSD([sQuery(id+"F0.wireOp",EDGE,"E25.0"),sQuery(id+"F0.wireOp",EDGE,"E25.1"),sQuery(id+"F0.wireOp",EDGE,"E25.2"),sQuery(id+"F0.wireOp",EDGE,"E25.3"),sQuery(id+"F0.wireOp",EDGE,"E25.4"),sQuery(id+"F0.wireOp",EDGE,"E25.5"),sQuery(id+"F0.wireOp",EDGE,"E25.6"),sQuery(id+"F0.wireOp",EDGE,"E25.7")])],"isStart":false})})});
            extrude(context, id + "F13", {"entities" : qUnion([Q0]), "operationType" : NewBodyOperationType.REMOVE, "endBound" : BoundingType.UP_TO_SURFACE, "endBoundEntityFace" : qUnion([Q1]), "depth" : 25 * mm});
        }
        {
            var Q0;
            Q0=makeQuery(id+"F3.boolean.opBoolean","COPY",EDGE,{"derivedFrom":makeQuery(id+"F3.opExtrude","CAP_EDGE",EDGE,{"disambiguationData":[OSD([sQuery(id+"F0.wireOp",EDGE,"E25.6")])],"isStart":false})});
            var Q1;
            Q1=makeQuery(id+"F8.boolean.opBoolean","INTERSECT",EDGE,{"derivedFrom":[makeQuery(id+"F5.opExtrude","SWEPT_FACE",FACE,{"disambiguationData":[OSD([sQuery(id+"F4.wireOp",EDGE,"E30")])]}),makeQuery(id+"F8.opExtrude","CAP_FACE",FACE,{"disambiguationData":[OSD([sQuery(id+"F7.wireOp",EDGE,"E67")])],"isStart":false})]});
            var Q2;
            Q2=makeQuery(id+"F8.boolean.opBoolean","INTERSECT",EDGE,{"disambiguationData":[OD(1.0)],"derivedFrom":[makeQuery(id+"F5.opExtrude","SWEPT_FACE",FACE,{"disambiguationData":[OSD([sQuery(id+"F4.wireOp",EDGE,"E30")])]}),makeQuery(id+"F8.opExtrude","SWEPT_FACE",FACE,{"disambiguationData":[OSD([sQuery(id+"F7.wireOp",EDGE,"E67")])]})]});
            var Q3;
            {var subQ0=sQuery(id+"F4.wireOp",EDGE,"E30");Q3=makeQuery(id+"F8.boolean.opBoolean","SPLIT",EDGE,{"disambiguationData":[TD([makeQuery(id+"F5.opExtrude","SWEPT_FACE",FACE,{"disambiguationData":[OSD([sQuery(id+"F4.wireOp",EDGE,"E35.filletArc")])]})])],"derivedFrom":makeQuery(id+"F5.opExtrude","CAP_EDGE",EDGE,{"disambiguationData":[OSD([subQ0])],"isStart":false})});}
            var Q4;
            {var subQ0=sQuery(id+"F0.wireOp",EDGE,"E25.7");var subQ1=sQuery(id+"F0.wireOp",EDGE,"E25.1");var subQ2=sQuery(id+"F0.wireOp",EDGE,"E25.6");var subQ3=sQuery(id+"F0.wireOp",EDGE,"E25.5");var subQ4=sQuery(id+"F0.wireOp",EDGE,"E25.4");var subQ5=sQuery(id+"F0.wireOp",EDGE,"E25.0");var subQ6=sQuery(id+"F0.wireOp",EDGE,"E25.2");var subQ7=sQuery(id+"F0.wireOp",EDGE,"E25.3");Q4=makeQuery(id+"F8.boolean.opBoolean","INTERSECT",EDGE,{"derivedFrom":[makeQuery(id+"F5.boolean.opBoolean","SPLIT",FACE,{"disambiguationData":[TD([makeQuery(id+"F2.opExtrude","SWEPT_FACE",FACE,{"disambiguationData":[OSD([subQ5])]})])],"derivedFrom":makeQuery(id+"F3.boolean.opBoolean","COPY",FACE,{"derivedFrom":makeQuery(id+"F3.opExtrude","CAP_FACE",FACE,{"disambiguationData":[OSD([subQ5,subQ1,subQ6,subQ7,subQ4,subQ3,subQ2,subQ0])],"isStart":false})})}),makeQuery(id+"F8.opExtrude","SWEPT_FACE",FACE,{"disambiguationData":[OSD([sQuery(id+"F7.wireOp",EDGE,"E67")])]})]});}
            var Q5;
            Q5=makeQuery(id+"F8.boolean.opBoolean","INTERSECT",EDGE,{"disambiguationData":[OD(0.0)],"derivedFrom":[makeQuery(id+"F5.opExtrude","SWEPT_FACE",FACE,{"disambiguationData":[OSD([sQuery(id+"F4.wireOp",EDGE,"E30")])]}),makeQuery(id+"F8.opExtrude","SWEPT_FACE",FACE,{"disambiguationData":[OSD([sQuery(id+"F7.wireOp",EDGE,"E67")])]})]});
            fillet(context, id + "F14", {"entities" : qUnion([Q0, Q1, Q2, Q3, Q4, Q5]), "radius" : 3 * mm, "tangentPropagation" : true, "allowEdgeOverflow" : false});
        }
        {
            var Q0;
            Q0=makeQuery(id+"F1.opExtrude","CAP_EDGE",EDGE,{"disambiguationData":[OSD([sQuery(id+"F0.wireOp",EDGE,"E1.bottom")])],"isStart":false});
            fillet(context, id + "F15", {"entities" : qUnion([Q0]), "radius" : 2 * mm, "tangentPropagation" : true, "allowEdgeOverflow" : false});
        }
        {
            var Q0;
            {var subQ0=sQuery(id+"F0.wireOp",EDGE,"E21.filletArc");var subQ1=sQuery(id+"F0.wireOp",EDGE,"E7");var subQ2=sQuery(id+"F0.wireOp",EDGE,"E6");var subQ3=sQuery(id+"F0.wireOp",EDGE,"E5");var subQ4=sQuery(id+"F0.wireOp",EDGE,"E4");var subQ5=sQuery(id+"F0.wireOp",EDGE,"E22.filletArc");var subQ6=sQuery(id+"F0.wireOp",EDGE,"E1.bottom");var subQ7=sQuery(id+"F0.wireOp",EDGE,"E1.right");var subQ8=sQuery(id+"F0.wireOp",EDGE,"E1.top");var subQ9=sQuery(id+"F0.wireOp",EDGE,"E1.left");var subQ10=sQuery(id+"F0.wireOp",EDGE,"E23.filletArc");var subQ11=sQuery(id+"F0.wireOp",EDGE,"E24.filletArc");Q0=makeQuery(id+"F2.boolean.opBoolean","SPLIT",FACE,{"disambiguationData":[TD([makeQuery(id+"F1.opExtrude","SWEPT_FACE",FACE,{"disambiguationData":[OSD([subQ6])]})])],"derivedFrom":makeQuery(id+"F1.opExtrude","CAP_FACE",FACE,{"disambiguationData":[OSD([subQ6,subQ8,subQ9,subQ7,subQ4,subQ3,subQ2,subQ1,subQ0,subQ5,subQ10,subQ11])],"isStart":true})});}
            var sketch = newSketch(context, id + "F16", { "sketchPlane" : qUnion([Q0])});
            skCircle(sketch, "E79", {"center": v(0, 120) * mm, "radius": 6 * mm});
            skArc(sketch, "E80", {"start": v(15, 120) * mm, "mid": v(0, 135) * mm, "end": v(-15, 120) * mm});
            skLineSegment(sketch, "E81", {"start": v(-15, 120) * mm, "end": v(-15, 108) * mm});
            skLineSegment(sketch, "E82", {"start": v(-15, 108) * mm, "end": v(-33, 90) * mm});
            skLineSegment(sketch, "E83", {"start": v(15, 120) * mm, "end": v(15, 108) * mm});
            skLineSegment(sketch, "E84", {"start": v(15, 108) * mm, "end": v(33, 90) * mm});
            skLineSegment(sketch, "E85", {"start": v(33, 90) * mm, "end": v(-33, 90) * mm});
            skLineSegment(sketch, "E86", {"start": v(0, 120) * mm, "end": v(0, 90) * mm, "construction": true});
            skLineSegment(sketch, "E87", {"start": v(-80, 0) * mm, "end": v(80, 0) * mm, "construction": true});
            skCircle(sketch, "E88.MirrorC", {"center": v(0, -120) * mm, "radius": 6 * mm});
            skLineSegment(sketch, "E89.MirrorCS", {"start": v(-15, -120) * mm, "end": v(-15, -108) * mm});
            skArc(sketch, "E90.MirrorCS", {"start": v(15, -120) * mm, "mid": v(0, -135) * mm, "end": v(-15, -120) * mm});
            skLineSegment(sketch, "E91.MirrorCS", {"start": v(-15, -108) * mm, "end": v(-33, -90) * mm});
            skLineSegment(sketch, "E92.MirrorCS", {"start": v(15, -108) * mm, "end": v(33, -90) * mm});
            skLineSegment(sketch, "E93.MirrorCS", {"start": v(0, -120) * mm, "end": v(0, -90) * mm, "construction": true});
            skLineSegment(sketch, "E94.MirrorCS", {"start": v(15, -120) * mm, "end": v(15, -108) * mm});
            skLineSegment(sketch, "E95.MirrorCS", {"start": v(33, -90) * mm, "end": v(-33, -90) * mm});
            skSolve(sketch);
        }
        {
            var Q0;
            Q0 = qSketchRegion(id + "F16", true);
            var Q1;
            {var subQ2=sQuery(id+"F16.wireOp",EDGE,"E95.MirrorCS");Q1=makeQuery(id+"F16.imprint","IMPRINT",FACE,{"disambiguationData":[TD([[makeQuery(id+"F16.imprint","IMPRINT",EDGE,{"derivedFrom":subQ2}),1.0]])]});}
            extrude(context, id + "F17", {"entities" : qUnion([Q0, Q1]), "depth" : 25 * mm, "offsetDistance" : 25 * mm});
        }
        {
            var Q0;
            Q0=makeQuery(id+"F17.opExtrude","SWEPT_BODY",BODY,{"disambiguationData":[OSD([sQuery(id+"F0.wireOp",EDGE,"E1.bottom"),sQuery(id+"F0.wireOp",EDGE,"E1.top"),sQuery(id+"F0.wireOp",EDGE,"E1.left"),sQuery(id+"F0.wireOp",EDGE,"E1.right"),sQuery(id+"F0.wireOp",EDGE,"E4"),sQuery(id+"F0.wireOp",EDGE,"E5"),sQuery(id+"F0.wireOp",EDGE,"E6"),sQuery(id+"F0.wireOp",EDGE,"E7"),sQuery(id+"F0.wireOp",EDGE,"E12"),sQuery(id+"F0.wireOp",EDGE,"E13"),sQuery(id+"F0.wireOp",EDGE,"E14"),sQuery(id+"F0.wireOp",EDGE,"E15"),sQuery(id+"F0.wireOp",EDGE,"E17.filletArc"),sQuery(id+"F0.wireOp",EDGE,"E18.filletArc"),sQuery(id+"F0.wireOp",EDGE,"E19.filletArc"),sQuery(id+"F0.wireOp",EDGE,"E20.filletArc"),sQuery(id+"F0.wireOp",EDGE,"E21.filletArc"),sQuery(id+"F0.wireOp",EDGE,"E22.filletArc"),sQuery(id+"F0.wireOp",EDGE,"E23.filletArc"),sQuery(id+"F0.wireOp",EDGE,"E24.filletArc"),sQuery(id+"F16.wireOp",EDGE,"E79"),sQuery(id+"F16.wireOp",EDGE,"E80"),sQuery(id+"F16.wireOp",EDGE,"E81"),sQuery(id+"F16.wireOp",EDGE,"E83"),sQuery(id+"F16.wireOp",EDGE,"E84"),sQuery(id+"F16.wireOp",EDGE,"E88.MirrorC"),sQuery(id+"F16.wireOp",EDGE,"E89.MirrorCS"),sQuery(id+"F16.wireOp",EDGE,"E90.MirrorCS"),sQuery(id+"F16.wireOp",EDGE,"E91.MirrorCS"),sQuery(id+"F16.wireOp",EDGE,"E92.MirrorCS"),sQuery(id+"F16.wireOp",EDGE,"E94.MirrorCS"),sQuery(id+"F16.wireOp",EDGE,"E82")])]});
            deleteBodies(context, id + "F18", {"entities" : qUnion([Q0])});
        }
        {
            var Q0;
            Q0=makeQuery(id+"F16.imprint","IMPRINT",FACE,{"disambiguationData":[TD([[makeQuery(id+"F16.imprint","IMPRINT",EDGE,{"derivedFrom":sQuery(id+"F16.wireOp",EDGE,"E79")}),-1.0]])]});
            var Q1;
            Q1=makeQuery(id+"F16.imprint","IMPRINT",FACE,{"disambiguationData":[TD([[makeQuery(id+"F16.imprint","IMPRINT",EDGE,{"derivedFrom":sQuery(id+"F16.wireOp",EDGE,"E88.MirrorC")}),1.0]])]});
            var Q2;
            {var subQ2=sQuery(id+"F16.wireOp",EDGE,"E95.MirrorCS");Q2=makeQuery(id+"F16.imprint","IMPRINT",FACE,{"disambiguationData":[TD([[makeQuery(id+"F16.imprint","IMPRINT",EDGE,{"derivedFrom":subQ2}),1.0]])]});}
            var Q3;
            Q3=makeQuery(id+"F2.opExtrude","CAP_FACE",FACE,{"disambiguationData":[OSD([sQuery(id+"F0.wireOp",EDGE,"E12"),sQuery(id+"F0.wireOp",EDGE,"E13"),sQuery(id+"F0.wireOp",EDGE,"E14"),sQuery(id+"F0.wireOp",EDGE,"E15"),sQuery(id+"F0.wireOp",EDGE,"E17.filletArc"),sQuery(id+"F0.wireOp",EDGE,"E18.filletArc"),sQuery(id+"F0.wireOp",EDGE,"E19.filletArc"),sQuery(id+"F0.wireOp",EDGE,"E20.filletArc"),sQuery(id+"F0.wireOp",EDGE,"E25.0"),sQuery(id+"F0.wireOp",EDGE,"E25.1"),sQuery(id+"F0.wireOp",EDGE,"E25.2"),sQuery(id+"F0.wireOp",EDGE,"E25.3"),sQuery(id+"F0.wireOp",EDGE,"E25.4"),sQuery(id+"F0.wireOp",EDGE,"E25.5"),sQuery(id+"F0.wireOp",EDGE,"E25.6"),sQuery(id+"F0.wireOp",EDGE,"E25.7")])],"isStart":false});
            extrude(context, id + "F19", {"entities" : qUnion([Q0, Q1, Q2]), "operationType" : NewBodyOperationType.ADD, "endBound" : BoundingType.UP_TO_SURFACE, "depth" : 25 * mm, "endBoundEntityFace" : qUnion([Q3]), "offsetDistance" : 25 * mm});
        }
    });
